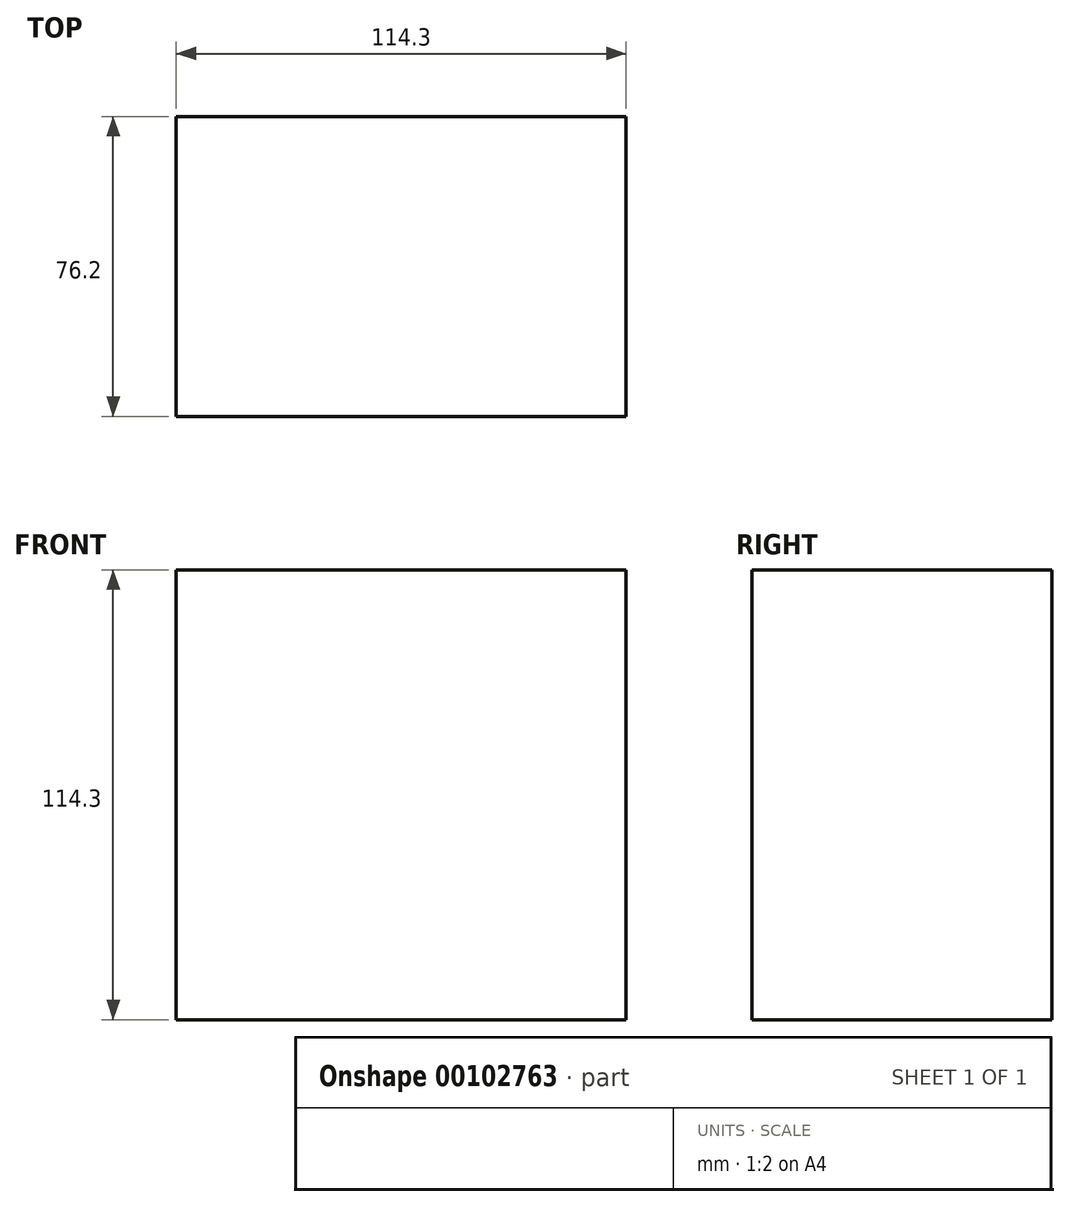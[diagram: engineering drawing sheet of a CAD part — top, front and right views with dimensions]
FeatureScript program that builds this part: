
annotation { "Feature Type Name" : "Feature", "Feature Type Description" : "" }
export const myFeature = defineFeature(function(context is Context, id is Id, definition is map)
    precondition{}
    {
        {
            var Q0;
            Q0=qCreatedBy(makeId("Front.planeOp"),FACE);
            var sketch = newSketch(context, id + "F0", { "sketchPlane" : qUnion([Q0])});
            skLineSegment(sketch, "E0.bottom", {"start": v(57.15, -57.15) * mm, "end": v(-57.15, -57.15) * mm});
            skLineSegment(sketch, "E0.top", {"start": v(57.15, 57.15) * mm, "end": v(-57.15, 57.15) * mm});
            skLineSegment(sketch, "E0.left", {"start": v(57.15, -57.15) * mm, "end": v(57.15, 57.15) * mm});
            skLineSegment(sketch, "E0.right", {"start": v(-57.15, -57.15) * mm, "end": v(-57.15, 57.15) * mm});
            skPoint(sketch, "E0.middle", {"position": v(0, 0) * mm});
            skSolve(sketch);
        }
        {
            var Q0;
            Q0=makeQuery(id+"F0.imprint","IMPRINT",FACE,{"disambiguationData":[TD([[makeQuery(id+"F0.imprint","IMPRINT",EDGE,{"derivedFrom":sQuery(id+"F0.wireOp",EDGE,"E0.bottom")}),-1.0]])]});
            extrude(context, id + "F1", {"entities" : qUnion([Q0]), "endBound" : BoundingType.SYMMETRIC, "depth" : 76.2 * mm});
        }
    });
